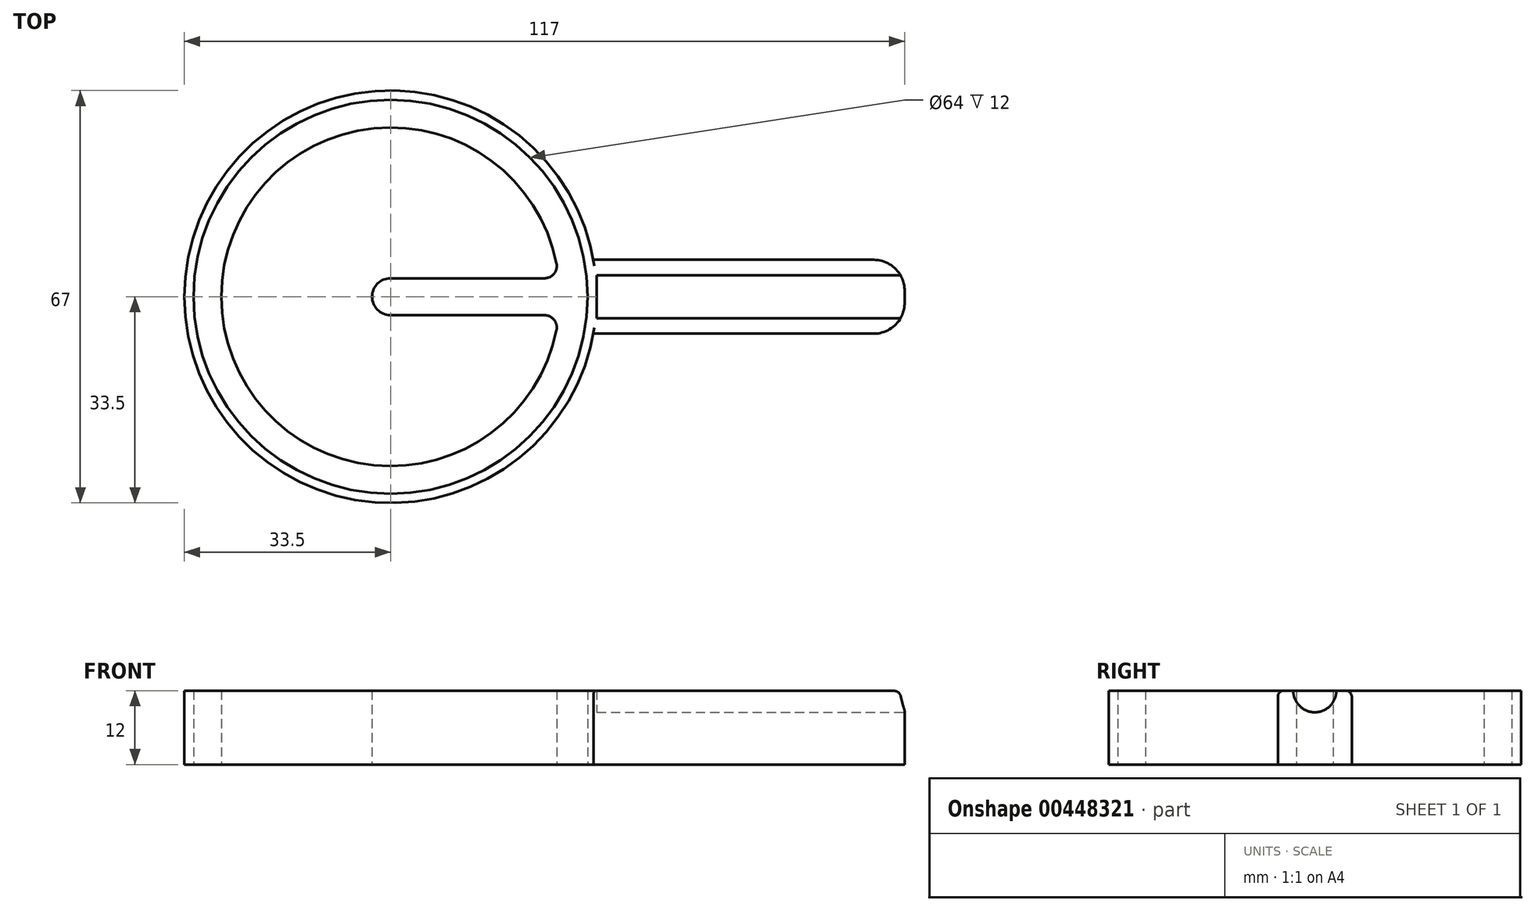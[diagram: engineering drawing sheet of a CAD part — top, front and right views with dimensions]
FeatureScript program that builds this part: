
annotation { "Feature Type Name" : "Feature", "Feature Type Description" : "" }
export const myFeature = defineFeature(function(context is Context, id is Id, definition is map)
    precondition{}
    {
        {
            var Q0;
            Q0=qCreatedBy(makeId("Top.planeOp"),FACE);
            var sketch = newSketch(context, id + "F0", { "sketchPlane" : qUnion([Q0])});
            skArc(sketch, "E0", {"start": v(27.34, 3) * mm, "mid": v(-27.5, 0) * mm, "end": v(27.34, -3) * mm});
            skArc(sketch, "E1", {"start": v(0, 3) * mm, "mid": v(-3, 0) * mm, "end": v(0, -3) * mm});
            skLineSegment(sketch, "E2.bottom", {"start": v(0, 3) * mm, "end": v(27.34, 3) * mm});
            skLineSegment(sketch, "E2.top", {"start": v(0, -3) * mm, "end": v(27.34, -3) * mm});
            skSolve(sketch);
        }
        {
            var Q0;
            Q0=makeQuery(id+"F0.imprint","IMPRINT",FACE,{"disambiguationData":[TD([[makeQuery(id+"F0.imprint","IMPRINT",EDGE,{"derivedFrom":sQuery(id+"F0.wireOp",EDGE,"E0")}),1.0]])]});
            extrude(context, id + "F1", {"entities" : qUnion([Q0]), "depth" : 12 * mm});
        }
        {
            var Q0;
            Q0=makeQuery(id+"F1.opExtrude","SWEPT_EDGE",EDGE,{"disambiguationData":[OSD([sQuery(id+"F0.wireOp",EDGE,"E0"),sQuery(id+"F0.wireOp",EDGE,"E2.bottom")])]});
            var Q1;
            Q1=makeQuery(id+"F1.opExtrude","SWEPT_EDGE",EDGE,{"disambiguationData":[OSD([sQuery(id+"F0.wireOp",EDGE,"E0"),sQuery(id+"F0.wireOp",EDGE,"E2.top")])]});
            fillet(context, id + "F2", {"entities" : qUnion([Q0, Q1]), "radius" : 2 * mm, "tangentPropagation" : true, "allowEdgeOverflow" : false});
        }
        {
            var Q0;
            Q0=qCreatedBy(makeId("Top.planeOp"),FACE);
            var sketch = newSketch(context, id + "F3", { "sketchPlane" : qUnion([Q0])});
            skCircle(sketch, "E3", {"center": v(0, 0) * mm, "radius": 32 * mm});
            skArc(sketch, "E4", {"start": v(32.96, 6) * mm, "mid": v(-33.5, 0) * mm, "end": v(32.96, -6) * mm});
            skLineSegment(sketch, "E5.bottom", {"start": v(32.96, -6) * mm, "end": v(83.5, -6) * mm});
            skLineSegment(sketch, "E5.top", {"start": v(32.96, 6) * mm, "end": v(83.5, 6) * mm});
            skLineSegment(sketch, "E5.right", {"start": v(83.5, -6) * mm, "end": v(83.5, 6) * mm});
            skSolve(sketch);
        }
        {
            var Q0;
            Q0=makeQuery(id+"F3.imprint","IMPRINT",FACE,{"disambiguationData":[TD([[makeQuery(id+"F3.imprint","IMPRINT",EDGE,{"derivedFrom":sQuery(id+"F3.wireOp",EDGE,"E3")}),-1.0]])]});
            extrude(context, id + "F4", {"entities" : qUnion([Q0]), "depth" : 12 * mm});
        }
        {
            var Q0;
            Q0=makeQuery(id+"F4.opExtrude","SWEPT_FACE",FACE,{"disambiguationData":[OSD([sQuery(id+"F3.wireOp",EDGE,"E5.right")])]});
            var sketch = newSketch(context, id + "F5", { "sketchPlane" : qUnion([Q0])});
            skCircle(sketch, "E6", {"center": v(0, 12) * mm, "radius": 3.5 * mm});
            skSolve(sketch);
        }
        {
            var Q0;
            {var subQ0=sQuery(id+"F5.wireOp",EDGE,"E6");var subQ1=makeQuery(id+"F4.opExtrude","CAP_EDGE",EDGE,{"disambiguationData":[OSD([sQuery(id+"F3.wireOp",EDGE,"E5.right")])],"isStart":false});var subQ2=makeQuery(id+"F5.imprint","INTERSECT",VERTEX,{"disambiguationData":[OD(0.0)],"derivedFrom":[subQ1,subQ0]});Q0=makeQuery(id+"F5.imprint","IMPRINT",FACE,{"disambiguationData":[TD([[makeQuery(id+"F5.imprint","IMPRINT",EDGE,{"disambiguationData":[TD([[subQ2,-1.0]])],"derivedFrom":subQ0}),1.0]])]});}
            extrude(context, id + "F6", {"entities" : qUnion([Q0]), "operationType" : NewBodyOperationType.REMOVE, "oppositeDirection" : true, "depth" : 50 * mm});
        }
        {
            var Q0;
            Q0=makeQuery(id+"F4.opExtrude","SWEPT_EDGE",EDGE,{"disambiguationData":[OSD([sQuery(id+"F3.wireOp",EDGE,"E5.bottom"),sQuery(id+"F3.wireOp",EDGE,"E5.right")])]});
            var Q1;
            Q1=makeQuery(id+"F4.opExtrude","SWEPT_EDGE",EDGE,{"disambiguationData":[OSD([sQuery(id+"F3.wireOp",EDGE,"E5.top"),sQuery(id+"F3.wireOp",EDGE,"E5.right")])]});
            fillet(context, id + "F7", {"entities" : qUnion([Q0, Q1]), "radius" : 5 * mm, "tangentPropagation" : true, "allowEdgeOverflow" : false});
        }
        {
            var Q0;
            Q0=makeQuery(id+"F4.opExtrude","CAP_EDGE",EDGE,{"disambiguationData":[OSD([sQuery(id+"F3.wireOp",EDGE,"E5.bottom")])],"isStart":false});
            var Q1;
            Q1=makeQuery(id+"F4.opExtrude","CAP_EDGE",EDGE,{"disambiguationData":[OSD([sQuery(id+"F3.wireOp",EDGE,"E5.top")])],"isStart":false});
            fillet(context, id + "F8", {"entities" : qUnion([Q0, Q1]), "radius" : 1 * mm, "tangentPropagation" : true, "allowEdgeOverflow" : false});
        }
    });
